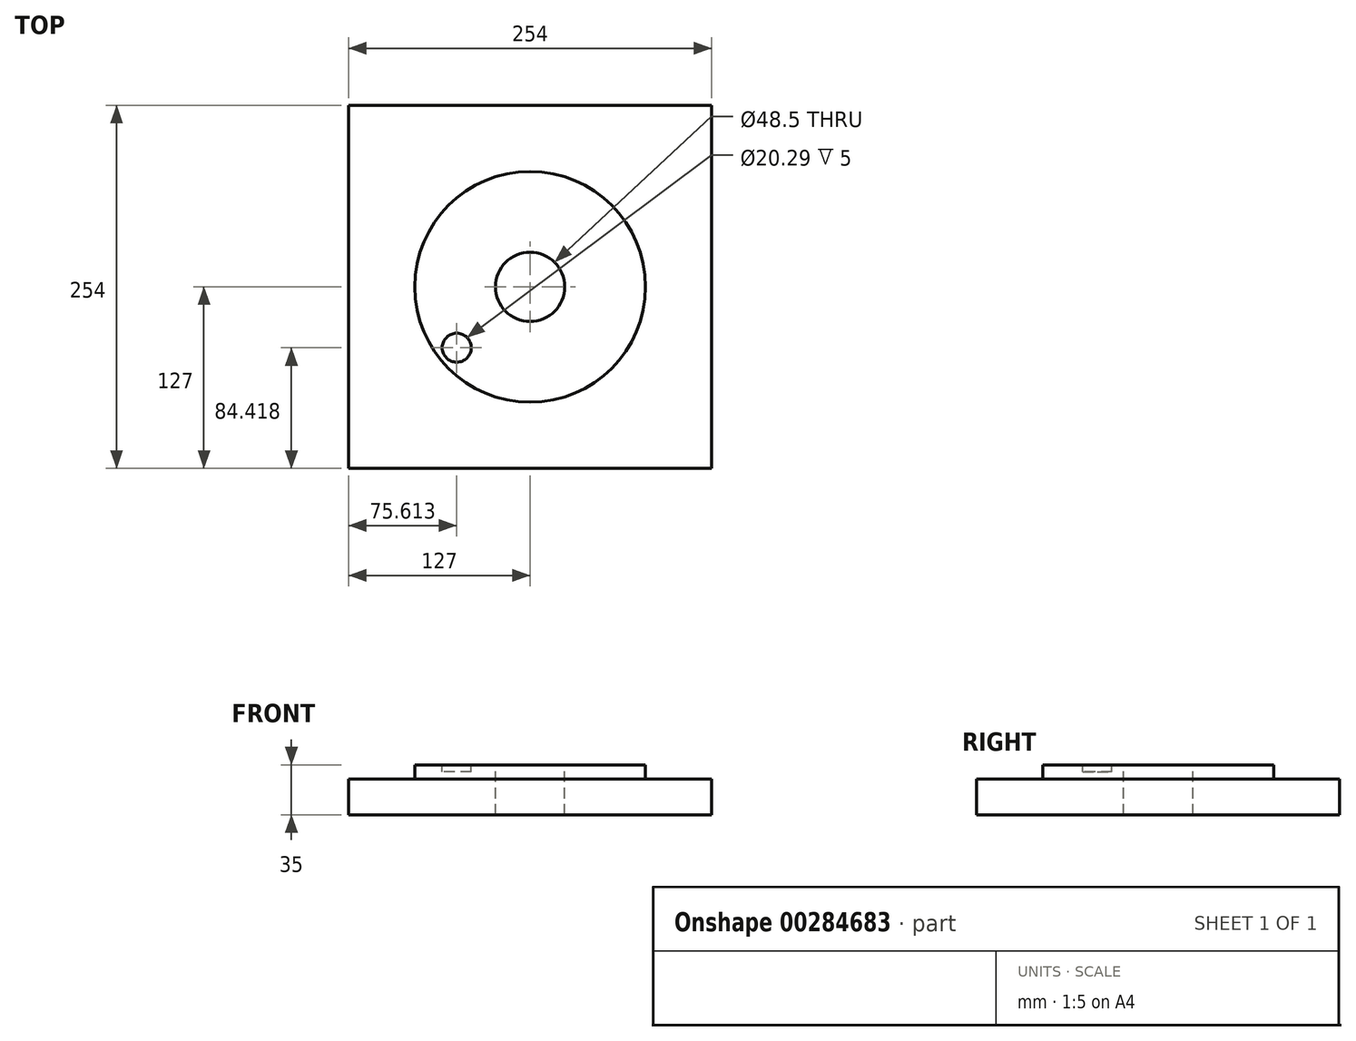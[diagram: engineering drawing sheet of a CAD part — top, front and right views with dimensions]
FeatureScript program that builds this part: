
annotation { "Feature Type Name" : "Feature", "Feature Type Description" : "" }
export const myFeature = defineFeature(function(context is Context, id is Id, definition is map)
    precondition{}
    {
        {
            var Q0;
            Q0=qCreatedBy(makeId("Top.planeOp"),FACE);
            var sketch = newSketch(context, id + "F0", { "sketchPlane" : qUnion([Q0])});
            skLineSegment(sketch, "E0.bottom", {"start": v(-127, 127) * mm, "end": v(127, 127) * mm});
            skLineSegment(sketch, "E0.top", {"start": v(-127, -127) * mm, "end": v(127, -127) * mm});
            skLineSegment(sketch, "E0.left", {"start": v(-127, 127) * mm, "end": v(-127, -127) * mm});
            skLineSegment(sketch, "E0.right", {"start": v(127, 127) * mm, "end": v(127, -127) * mm});
            skPoint(sketch, "E0.middle", {"position": v(0, 0) * mm});
            skSolve(sketch);
        }
        {
            var Q0;
            Q0 = qSketchRegion(id + "F0", true);
            extrude(context, id + "F1", {"entities" : qUnion([Q0]), "depth" : 25 * mm});
        }
        {
            var Q0;
            Q0=makeQuery(id+"F1.opExtrude","CAP_FACE",FACE,{"disambiguationData":[OSD([sQuery(id+"F0.wireOp",EDGE,"E0.bottom"),sQuery(id+"F0.wireOp",EDGE,"E0.top"),sQuery(id+"F0.wireOp",EDGE,"E0.left"),sQuery(id+"F0.wireOp",EDGE,"E0.right")])],"isStart":false});
            var sketch = newSketch(context, id + "F2", { "sketchPlane" : qUnion([Q0])});
            skCircle(sketch, "E1", {"center": v(0, 0) * mm, "radius": 80.73 * mm});
            skSolve(sketch);
        }
        {
            var Q0;
            Q0 = qSketchRegion(id + "F2", true);
            extrude(context, id + "F3", {"entities" : qUnion([Q0]), "operationType" : NewBodyOperationType.ADD, "depth" : 10 * mm});
        }
        {
            var Q0;
            Q0=makeQuery(id+"F3.opExtrude","CAP_FACE",FACE,{"disambiguationData":[OSD([sQuery(id+"F2.wireOp",EDGE,"E1")])],"isStart":false});
            var sketch = newSketch(context, id + "F4", { "sketchPlane" : qUnion([Q0])});
            skCircle(sketch, "E2", {"center": v(0, 0) * mm, "radius": 24.25 * mm});
            skSolve(sketch);
        }
        {
            var Q0;
            Q0=makeQuery(id+"F4.imprint","IMPRINT",FACE,{"disambiguationData":[TD([[makeQuery(id+"F4.imprint","IMPRINT",EDGE,{"derivedFrom":sQuery(id+"F4.wireOp",EDGE,"E2")}),1.0]])]});
            extrude(context, id + "F5", {"entities" : qUnion([Q0]), "operationType" : NewBodyOperationType.REMOVE, "oppositeDirection" : true, "depth" : 1270 * mm});
        }
        {
            var Q0;
            Q0=makeQuery(id+"F3.opExtrude","CAP_FACE",FACE,{"disambiguationData":[OSD([sQuery(id+"F2.wireOp",EDGE,"E1")])],"isStart":false});
            var sketch = newSketch(context, id + "F6", { "sketchPlane" : qUnion([Q0])});
            skCircle(sketch, "E3", {"center": v(-51.39, -42.58) * mm, "radius": 10.15 * mm});
            skSolve(sketch);
        }
        {
            var Q0;
            Q0 = qSketchRegion(id + "F6", true);
            extrude(context, id + "F7", {"entities" : qUnion([Q0]), "operationType" : NewBodyOperationType.REMOVE, "oppositeDirection" : true, "depth" : 5 * mm});
        }
    });
